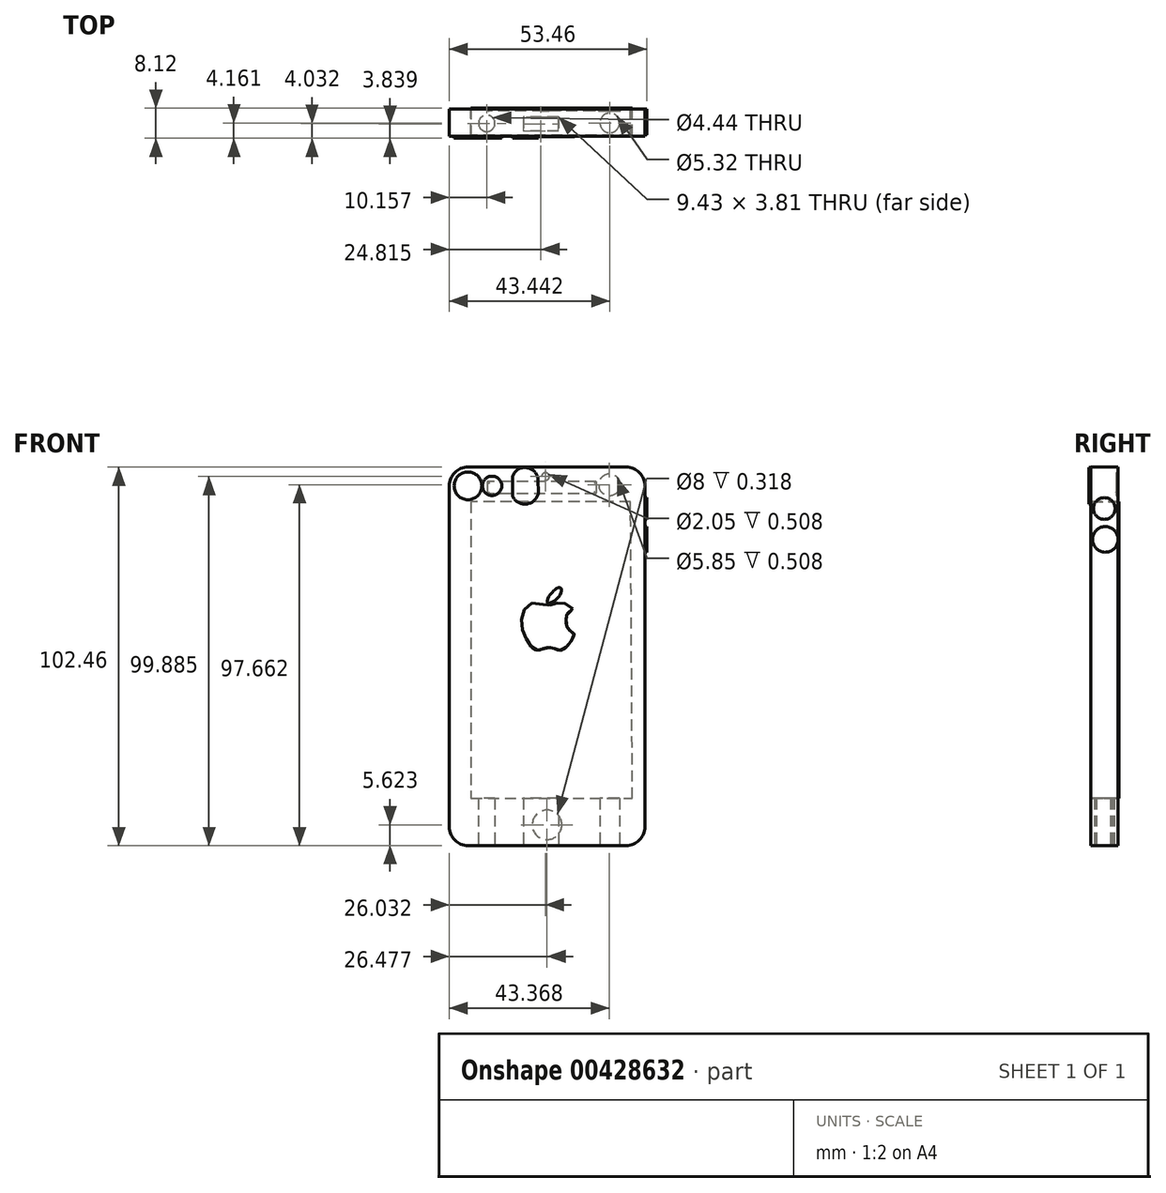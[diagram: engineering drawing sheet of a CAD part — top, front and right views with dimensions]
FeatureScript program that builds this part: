
annotation { "Feature Type Name" : "Feature", "Feature Type Description" : "" }
export const myFeature = defineFeature(function(context is Context, id is Id, definition is map)
    precondition{}
    {
        {
            var Q0;
            Q0=qCreatedBy(makeId("Front.planeOp"),FACE);
            var sketch = newSketch(context, id + "F0", { "sketchPlane" : qUnion([Q0])});
            skLineSegment(sketch, "E0.bottom", {"start": v(-45.76, 50.08) * mm, "end": v(7.2, 50.08) * mm});
            skLineSegment(sketch, "E0.top", {"start": v(-45.76, -52.38) * mm, "end": v(7.2, -52.38) * mm});
            skLineSegment(sketch, "E0.left", {"start": v(-45.76, 50.08) * mm, "end": v(-45.76, -52.38) * mm});
            skLineSegment(sketch, "E0.right", {"start": v(7.2, 50.08) * mm, "end": v(7.2, -52.38) * mm});
            skSolve(sketch);
        }
        {
            var Q0;
            Q0=makeQuery(id+"F0.imprint","IMPRINT",FACE,{"disambiguationData":[TD([[makeQuery(id+"F0.imprint","IMPRINT",EDGE,{"derivedFrom":sQuery(id+"F0.wireOp",EDGE,"E0.bottom")}),-1.0]])]});
            extrude(context, id + "F1", {"entities" : qUnion([Q0]), "depth" : 7.37 * mm});
        }
        {
            var Q0;
            Q0=makeQuery(id+"F1.opExtrude","SWEPT_EDGE",EDGE,{"disambiguationData":[OSD([sQuery(id+"F0.wireOp",EDGE,"E0.bottom"),sQuery(id+"F0.wireOp",EDGE,"E0.left")])]});
            var Q1;
            Q1=makeQuery(id+"F1.opExtrude","SWEPT_EDGE",EDGE,{"disambiguationData":[OSD([sQuery(id+"F0.wireOp",EDGE,"E0.bottom"),sQuery(id+"F0.wireOp",EDGE,"E0.right")])]});
            var Q2;
            Q2=makeQuery(id+"F1.opExtrude","SWEPT_EDGE",EDGE,{"disambiguationData":[OSD([sQuery(id+"F0.wireOp",EDGE,"E0.top"),sQuery(id+"F0.wireOp",EDGE,"E0.right")])]});
            var Q3;
            Q3=makeQuery(id+"F1.opExtrude","SWEPT_EDGE",EDGE,{"disambiguationData":[OSD([sQuery(id+"F0.wireOp",EDGE,"E0.top"),sQuery(id+"F0.wireOp",EDGE,"E0.left")])]});
            fillet(context, id + "F2", {"entities" : qUnion([Q0, Q1, Q2, Q3]), "radius" : 5.08 * mm, "tangentPropagation" : true, "allowEdgeOverflow" : false});
        }
        {
            var Q0;
            Q0=makeQuery(id+"F1.opExtrude","CAP_FACE",FACE,{"disambiguationData":[OSD([sQuery(id+"F0.wireOp",EDGE,"E0.bottom"),sQuery(id+"F0.wireOp",EDGE,"E0.top"),sQuery(id+"F0.wireOp",EDGE,"E0.left"),sQuery(id+"F0.wireOp",EDGE,"E0.right")])],"isStart":true});
            var sketch = newSketch(context, id + "F3", { "sketchPlane" : qUnion([Q0])});
            skLineSegment(sketch, "E1", {"start": v(-7.2, 40.58) * mm, "end": v(45.76, 40.58) * mm});
            skLineSegment(sketch, "E2", {"start": v(-7.2, -41.73) * mm, "end": v(45.76, -41.73) * mm});
            skCircle(sketch, "E3", {"center": v(19.28, -46.76) * mm, "radius": 4 * mm});
            skPoint(sketch, "E3.centerSnap0", {"position": v(19.28, -52.38) * mm});
            skSolve(sketch);
        }
        {
            var Q0;
            Q0=makeQuery(id+"F1.opExtrude","SWEPT_FACE",FACE,{"disambiguationData":[OSD([sQuery(id+"F0.wireOp",EDGE,"E0.top")])]});
            var sketch = newSketch(context, id + "F4", { "sketchPlane" : qUnion([Q0])});
            skLineSegment(sketch, "E4.bottom", {"start": v(-16.23, 2.13) * mm, "end": v(-25.66, 2.13) * mm});
            skLineSegment(sketch, "E4.top", {"start": v(-16.23, 5.94) * mm, "end": v(-25.66, 5.94) * mm});
            skLineSegment(sketch, "E4.left", {"start": v(-16.23, 2.13) * mm, "end": v(-16.23, 5.94) * mm});
            skLineSegment(sketch, "E4.right", {"start": v(-25.66, 2.13) * mm, "end": v(-25.66, 5.94) * mm});
            skCircle(sketch, "E5", {"center": v(-35.6, 3.84) * mm, "radius": 2.22 * mm});
            skCircle(sketch, "E6", {"center": v(-2.32, 3.7) * mm, "radius": 2.66 * mm});
            skSolve(sketch);
        }
        {
            var Q0;
            Q0=makeQuery(id+"F4.imprint","IMPRINT",FACE,{"disambiguationData":[TD([[makeQuery(id+"F4.imprint","IMPRINT",EDGE,{"derivedFrom":sQuery(id+"F4.wireOp",EDGE,"E6")}),1.0]])]});
            var Q1;
            Q1=makeQuery(id+"F4.imprint","IMPRINT",FACE,{"disambiguationData":[TD([[makeQuery(id+"F4.imprint","IMPRINT",EDGE,{"derivedFrom":sQuery(id+"F4.wireOp",EDGE,"E4.bottom")}),-1.0]])]});
            var Q2;
            Q2=makeQuery(id+"F4.imprint","IMPRINT",FACE,{"disambiguationData":[TD([[makeQuery(id+"F4.imprint","IMPRINT",EDGE,{"derivedFrom":sQuery(id+"F4.wireOp",EDGE,"E5")}),1.0]])]});
            extrude(context, id + "F5", {"entities" : qUnion([Q0, Q1, Q2]), "operationType" : NewBodyOperationType.REMOVE, "oppositeDirection" : true, "depth" : 25.4 * mm});
        }
        {
            var Q0;
            Q0=makeQuery(id+"F3.imprint","IMPRINT",FACE,{"disambiguationData":[TD([[makeQuery(id+"F3.imprint","IMPRINT",EDGE,{"derivedFrom":sQuery(id+"F3.wireOp",EDGE,"E3")}),1.0]])]});
            extrude(context, id + "F6", {"entities" : qUnion([Q0]), "operationType" : NewBodyOperationType.REMOVE, "oppositeDirection" : true, "depth" : 0.32 * mm});
        }
        {
            var Q0;
            Q0=makeQuery(id+"F1.opExtrude","CAP_FACE",FACE,{"disambiguationData":[OSD([sQuery(id+"F0.wireOp",EDGE,"E0.bottom"),sQuery(id+"F0.wireOp",EDGE,"E0.top"),sQuery(id+"F0.wireOp",EDGE,"E0.left"),sQuery(id+"F0.wireOp",EDGE,"E0.right")])],"isStart":true});
            var sketch = newSketch(context, id + "F7", { "sketchPlane" : qUnion([Q0])});
            skLineSegment(sketch, "E7", {"start": v(-3.3, 40.64) * mm, "end": v(39.88, 40.64) * mm});
            skLineSegment(sketch, "E8", {"start": v(39.88, 40.64) * mm, "end": v(39.88, -39.63) * mm});
            skLineSegment(sketch, "E9", {"start": v(39.88, -39.63) * mm, "end": v(-3.8, -39.63) * mm});
            skLineSegment(sketch, "E10", {"start": v(-3.8, -39.63) * mm, "end": v(-3.3, 40.64) * mm});
            skSolve(sketch);
        }
        {
            var Q0;
            Q0=makeQuery(id+"F7.imprint","IMPRINT",FACE,{"disambiguationData":[TD([[makeQuery(id+"F7.imprint","IMPRINT",EDGE,{"derivedFrom":sQuery(id+"F7.wireOp",EDGE,"E7")}),-1.0]])]});
            extrude(context, id + "F8", {"entities" : qUnion([Q0]), "operationType" : NewBodyOperationType.REMOVE, "oppositeDirection" : true, "depth" : 7.11 * mm});
        }
        {
            var Q0;
            Q0=makeQuery(id+"F1.opExtrude","CAP_FACE",FACE,{"disambiguationData":[OSD([sQuery(id+"F0.wireOp",EDGE,"E0.bottom"),sQuery(id+"F0.wireOp",EDGE,"E0.top"),sQuery(id+"F0.wireOp",EDGE,"E0.left"),sQuery(id+"F0.wireOp",EDGE,"E0.right")])],"isStart":false});
            var sketch = newSketch(context, id + "F9", { "sketchPlane" : qUnion([Q0])});
            skLineSegment(sketch, "E11", {"start": v(-45.76, 39.62) * mm, "end": v(7.2, 39.62) * mm});
            skCircle(sketch, "E12", {"center": v(-40.68, 45) * mm, "radius": 3.75 * mm});
            skArc(sketch, "E13", {"start": v(-21.76, 46.87) * mm, "mid": v(-24.92, 49.94) * mm, "end": v(-28.63, 47.57) * mm});
            skLineSegment(sketch, "E14", {"start": v(-28.63, 47.57) * mm, "end": v(-28.63, 42.22) * mm});
            skArc(sketch, "E15", {"start": v(-28.63, 42.22) * mm, "mid": v(-24.93, 40.09) * mm, "end": v(-21.66, 42.83) * mm});
            skLineSegment(sketch, "E16", {"start": v(-21.76, 46.87) * mm, "end": v(-21.66, 42.83) * mm});
            skCircle(sketch, "E17", {"center": v(-34.16, 45) * mm, "radius": 2.62 * mm});
            skSolve(sketch);
        }
        {
            var Q0;
            Q0=makeQuery(id+"F9.imprint","IMPRINT",FACE,{"disambiguationData":[TD([[makeQuery(id+"F9.imprint","IMPRINT",EDGE,{"derivedFrom":sQuery(id+"F9.wireOp",EDGE,"E12")}),1.0]])]});
            extrude(context, id + "F10", {"entities" : qUnion([Q0]), "operationType" : NewBodyOperationType.ADD, "depth" : 0.5 * mm});
        }
        {
            var Q0;
            Q0 = qSketchRegion(id + "F9", true);
            extrude(context, id + "F11", {"entities" : qUnion([Q0]), "operationType" : NewBodyOperationType.ADD, "depth" : 0.5 * mm});
        }
        {
            var Q0;
            Q0=makeQuery(id+"F8.boolean.opBoolean","COPY",FACE,{"derivedFrom":makeQuery(id+"F8.opExtrude","CAP_FACE",FACE,{"disambiguationData":[OSD([sQuery(id+"F7.wireOp",EDGE,"E7"),sQuery(id+"F7.wireOp",EDGE,"E8"),sQuery(id+"F7.wireOp",EDGE,"E9"),sQuery(id+"F7.wireOp",EDGE,"E10")])],"isStart":false})});
            var sketch = newSketch(context, id + "F12", { "sketchPlane" : qUnion([Q0])});
            skSolve(sketch);
        }
        {
            var Q0;
            Q0=makeQuery(id+"F12.imprint","IMPRINT",FACE,{"disambiguationData":[TD([[makeQuery(id+"F12.imprint","IMPRINT",EDGE,{"derivedFrom":makeQuery(id+"F8.boolean.opBoolean","COPY",EDGE,{"derivedFrom":makeQuery(id+"F8.opExtrude","CAP_EDGE",EDGE,{"disambiguationData":[OSD([sQuery(id+"F7.wireOp",EDGE,"E7")])],"isStart":false})})}),-1.0]])]});
            extrude(context, id + "F13", {"entities" : qUnion([Q0]), "depth" : 7.37 * mm});
        }
        {
            var Q0;
            Q0=makeQuery(id+"F1.opExtrude","CAP_FACE",FACE,{"disambiguationData":[OSD([sQuery(id+"F0.wireOp",EDGE,"E0.bottom"),sQuery(id+"F0.wireOp",EDGE,"E0.top"),sQuery(id+"F0.wireOp",EDGE,"E0.left"),sQuery(id+"F0.wireOp",EDGE,"E0.right")])],"isStart":true});
            var sketch = newSketch(context, id + "F14", { "sketchPlane" : qUnion([Q0])});
            skCircle(sketch, "E18", {"center": v(19.73, 47.5) * mm, "radius": 1.02 * mm});
            skCircle(sketch, "E19", {"center": v(2.4, 45.28) * mm, "radius": 2.93 * mm});
            skLineSegment(sketch, "E20.bottom", {"start": v(6.01, 46.17) * mm, "end": v(35.41, 46.17) * mm});
            skLineSegment(sketch, "E20.top", {"start": v(6.01, 42.87) * mm, "end": v(35.41, 42.87) * mm});
            skLineSegment(sketch, "E20.left", {"start": v(6.01, 46.17) * mm, "end": v(6.01, 42.87) * mm});
            skLineSegment(sketch, "E20.right", {"start": v(35.41, 46.17) * mm, "end": v(35.41, 42.87) * mm});
            skSolve(sketch);
        }
        {
            var Q0;
            Q0=makeQuery(id+"F14.imprint","IMPRINT",FACE,{"disambiguationData":[TD([[makeQuery(id+"F14.imprint","IMPRINT",EDGE,{"derivedFrom":sQuery(id+"F14.wireOp",EDGE,"E19")}),1.0]])]});
            var Q1;
            Q1=makeQuery(id+"F14.imprint","IMPRINT",FACE,{"disambiguationData":[TD([[makeQuery(id+"F14.imprint","IMPRINT",EDGE,{"derivedFrom":sQuery(id+"F14.wireOp",EDGE,"E20.bottom")}),-1.0]])]});
            var Q2;
            Q2=makeQuery(id+"F14.imprint","IMPRINT",FACE,{"disambiguationData":[TD([[makeQuery(id+"F14.imprint","IMPRINT",EDGE,{"derivedFrom":sQuery(id+"F14.wireOp",EDGE,"E18")}),1.0]])]});
            extrude(context, id + "F15", {"entities" : qUnion([Q0, Q1, Q2]), "operationType" : NewBodyOperationType.REMOVE, "oppositeDirection" : true, "depth" : 0.5 * mm});
        }
        {
            var Q0;
            Q0=makeQuery(id+"F15.boolean.opBoolean","COPY",EDGE,{"derivedFrom":makeQuery(id+"F15.opExtrude","CAP_EDGE",EDGE,{"disambiguationData":[OSD([sQuery(id+"F14.wireOp",EDGE,"E20.left")])],"isStart":true})});
            var Q1;
            Q1=makeQuery(id+"F15.boolean.opBoolean","COPY",EDGE,{"derivedFrom":makeQuery(id+"F15.opExtrude","CAP_EDGE",EDGE,{"disambiguationData":[OSD([sQuery(id+"F14.wireOp",EDGE,"E20.bottom")])],"isStart":true})});
            var Q2;
            Q2=makeQuery(id+"F15.boolean.opBoolean","COPY",EDGE,{"derivedFrom":makeQuery(id+"F15.opExtrude","CAP_EDGE",EDGE,{"disambiguationData":[OSD([sQuery(id+"F14.wireOp",EDGE,"E20.top")])],"isStart":true})});
            var Q3;
            Q3=makeQuery(id+"F15.boolean.opBoolean","COPY",FACE,{"derivedFrom":makeQuery(id+"F15.opExtrude","CAP_FACE",FACE,{"disambiguationData":[OSD([sQuery(id+"F14.wireOp",EDGE,"E20.bottom"),sQuery(id+"F14.wireOp",EDGE,"E20.top"),sQuery(id+"F14.wireOp",EDGE,"E20.left"),sQuery(id+"F14.wireOp",EDGE,"E20.right")])],"isStart":false})});
            var Q4;
            Q4=makeQuery(id+"F15.boolean.opBoolean","COPY",EDGE,{"derivedFrom":makeQuery(id+"F15.opExtrude","CAP_EDGE",EDGE,{"disambiguationData":[OSD([sQuery(id+"F14.wireOp",EDGE,"E20.right")])],"isStart":true})});
            fillet(context, id + "F16", {"entities" : qUnion([Q0, Q1, Q2, Q3, Q4]), "radius" : 0.5 * mm, "tangentPropagation" : true, "allowEdgeOverflow" : false});
        }
        {
            var Q0;
            Q0=makeQuery(id+"F1.opExtrude","CAP_FACE",FACE,{"disambiguationData":[OSD([sQuery(id+"F0.wireOp",EDGE,"E0.bottom"),sQuery(id+"F0.wireOp",EDGE,"E0.top"),sQuery(id+"F0.wireOp",EDGE,"E0.left"),sQuery(id+"F0.wireOp",EDGE,"E0.right")])],"isStart":false});
            var sketch = newSketch(context, id + "F17", { "sketchPlane" : qUnion([Q0])});
            skFitSpline(sketch, "E21", {"points": [v(-12.31, 11.7) * mm, v(-13.7, 10.5) * mm, v(-14.15, 9.2) * mm, v(-14.12, 7.82) * mm, v(-13.63, 6.36) * mm, v(-12.6, 5.42) * mm, v(-11.9, 4.94) * mm, v(-11.96, 4.9) * mm, v(-12.29, 3.7) * mm, v(-13.48, 2.09) * mm, v(-14.76, 0.8) * mm, v(-15.8, 0.48) * mm, v(-16.87, 0.76) * mm, v(-18.2, 1.18) * mm, v(-19.43, 1.14) * mm, v(-20.59, 0.8) * mm, v(-21.5, 0.52) * mm, v(-22.94, 0.97) * mm, v(-24.22, 2.38) * mm, v(-25.46, 4.85) * mm, v(-26.25, 8.07) * mm, v(-25.46, 11.34) * mm, v(-23.02, 13.28) * mm, v(-19.22, 12.58) * mm, v(-18.15, 12.78) * mm, v(-16.54, 13.32) * mm, v(-14.68, 13.24) * mm, v(-12.31, 11.7) * mm]});
            skFitSpline(sketch, "E22", {"points": [v(-17.78, 16.25) * mm, v(-17.08, 17) * mm, v(-15.63, 17.4) * mm, v(-15.6, 15.92) * mm, v(-16.38, 14.64) * mm, v(-17.78, 13.57) * mm, v(-19.18, 13.36) * mm, v(-18.77, 15.1) * mm, v(-17.78, 16.25) * mm]});
            skSolve(sketch);
        }
        {
            var Q0;
            Q0=makeQuery(id+"F17.imprint","IMPRINT",FACE,{"disambiguationData":[TD([[makeQuery(id+"F17.imprint","IMPRINT",EDGE,{"derivedFrom":sQuery(id+"F17.wireOp",EDGE,"E21")}),-1.0]])]});
            var Q1;
            Q1=makeQuery(id+"F17.imprint","IMPRINT",FACE,{"disambiguationData":[TD([[makeQuery(id+"F17.imprint","IMPRINT",EDGE,{"derivedFrom":sQuery(id+"F17.wireOp",EDGE,"E22")}),-1.0]])]});
            extrude(context, id + "F18", {"entities" : qUnion([Q0, Q1]), "operationType" : NewBodyOperationType.ADD, "depth" : 0.05 * mm});
        }
        {
            var Q0;
            Q0=makeQuery(id+"F1.opExtrude","SWEPT_FACE",FACE,{"disambiguationData":[OSD([sQuery(id+"F0.wireOp",EDGE,"E0.right")])]});
            var sketch = newSketch(context, id + "F19", { "sketchPlane" : qUnion([Q0])});
            skCircle(sketch, "E23", {"center": v(-3.74, 38.85) * mm, "radius": 2.94 * mm});
            skCircle(sketch, "E24", {"center": v(-3.45, 30.5) * mm, "radius": 3.47 * mm});
            skSolve(sketch);
        }
        {
            var Q0;
            Q0=makeQuery(id+"F19.imprint","IMPRINT",FACE,{"disambiguationData":[TD([[makeQuery(id+"F19.imprint","IMPRINT",EDGE,{"derivedFrom":sQuery(id+"F19.wireOp",EDGE,"E23")}),1.0]])]});
            var Q1;
            {var subQ0=sQuery(id+"F19.wireOp",EDGE,"E24");var subQ1=makeQuery(id+"F1.opExtrude","CAP_EDGE",EDGE,{"disambiguationData":[OSD([sQuery(id+"F0.wireOp",EDGE,"E0.right")])],"isStart":true});var subQ2=makeQuery(id+"F19.imprint","INTERSECT",VERTEX,{"disambiguationData":[OD(0.0)],"derivedFrom":[subQ1,subQ0]});Q1=makeQuery(id+"F19.imprint","IMPRINT",FACE,{"disambiguationData":[TD([[makeQuery(id+"F19.imprint","IMPRINT",EDGE,{"disambiguationData":[TD([[subQ2,-1.0]])],"derivedFrom":subQ0}),1.0]])]});}
            extrude(context, id + "F20", {"entities" : qUnion([Q0, Q1]), "operationType" : NewBodyOperationType.ADD, "depth" : 0.5 * mm});
        }
    });
